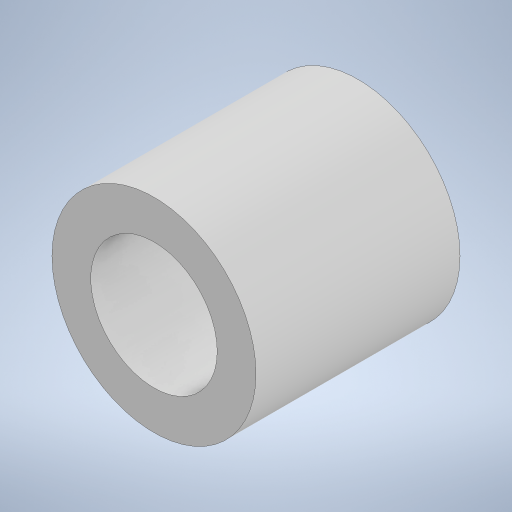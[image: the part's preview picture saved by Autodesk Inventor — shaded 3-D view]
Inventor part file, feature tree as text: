
AUTODESK INVENTOR PART (.ipt)
format: ipt  version: 2023 (Build 270158000, 158)  size: 208,896 bytes
history: native  units: in
note: dims shown in document units (in); Inventor stores cm internally (conversion verified against a paired STEP export)
features: extrude x1, sketch x1
ambient origin geometry x8: Origin, YZ Plane, XZ Plane, XY Plane, X Axis, Y Axis, Z Axis, Center Point
bodies: Solid1 (feature_tree)
feature tree (2):
  extrude  "Extrusion1"  Depth=0.3937in
  sketch  "Sketch1"  dims[d0=0.2441in d1=0.3937in d2=0.3937in d3=0.0in]
